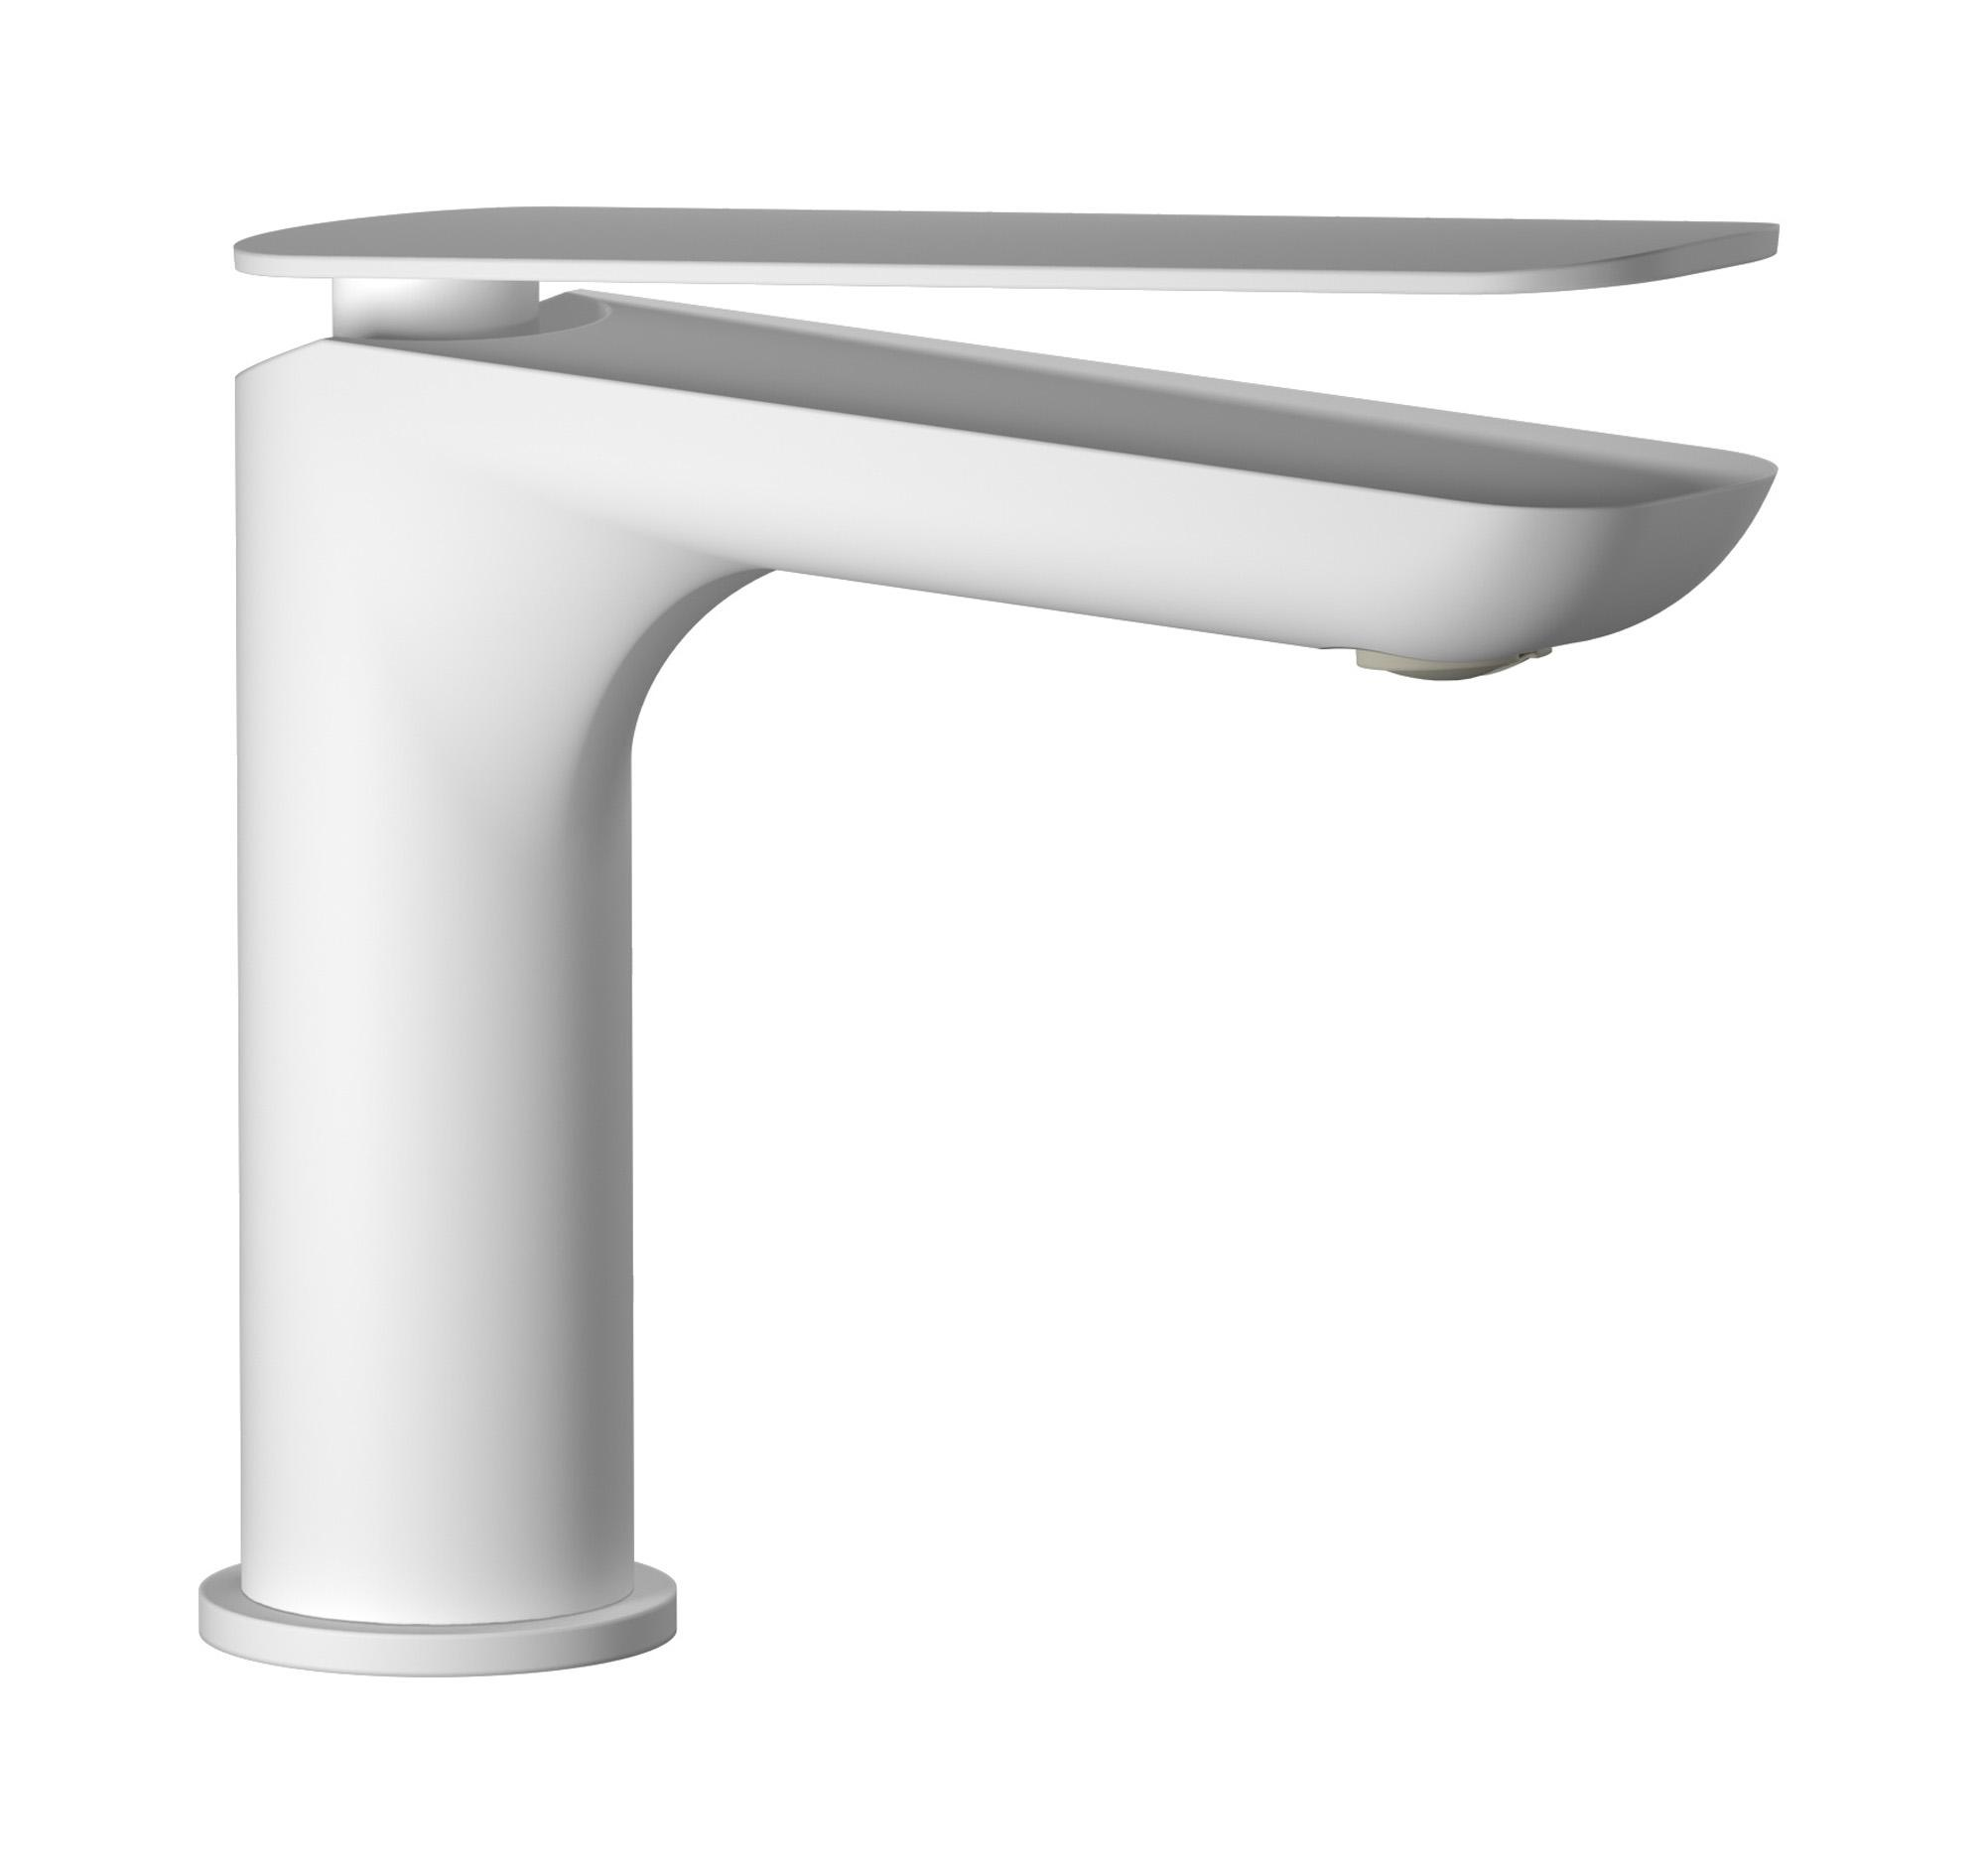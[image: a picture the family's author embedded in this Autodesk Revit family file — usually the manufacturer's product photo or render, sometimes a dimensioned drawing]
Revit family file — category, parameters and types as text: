
# Revit family: K2200
name_source: partatom
category: Apparecchi idraulici
units: mm (PartAtom-declared; Revit-internal decimal feet)

## family parameters
Basato su piano di lavoro = No
Condiviso = No
Mantieni orientamento annotazione = No
Numero OmniClass = 23.45.55.17
Punto di calcolo locali = No
Quota connettore circolare = Usa diametro
Sempre verticale = Sì
Taglio con vuoti quando caricato = No
Tipo di parte = Normale
Titolo OmniClass = Mixing Faucets

## types (9) — shared parameters
Cold water inlet = 10 mm  [stored 0.0328084 ft]
Commenti sul tipo = Washbasin mixer
Connessione CW = No
Connessione HW = No
Connessione di scarico = No
Connessione di ventilazione = No
Descrizione = Monohole washbasin mixer complete with drain
Hot water inlet = 10 mm  [stored 0.0328084 ft]
Produttore = IB Rubinetterie S.p.A.
URL = https://www.weareib.it
zero-valued in all types: Prospetto di default

## per-type parameters (varying)
| type | Finishes surface | Immagine tipo | Modello |
| Chrome | IB_Chrome | K2200CC.jpg | K2200CC |
| Brushed nickel | IB_Brushed nickel | K2200SS.jpg | K2200SS |
| Platinum | IB_Platinum | K2200PL.jpg | K2200PL |
| Matt white | IB_matt white | K2200BO.jpg | K2200BO |
| Matt black | IB_matt black | K2200NP.jpg | K2200NP |
| Pale gold | IB_Pale gold | K2200II.jpg | K2200II |
| Brushed pale gold | IB_brushed pale gold | K2200IS.jpg | K2200IS |
| Rose gold | IB_Rose gold | K2200RS.jpg | K2200RS |
| Gold | IB_gold | K2200OO.jpg | K2200OO |

note: [stored X ft] marks values corroborated as IEEE doubles in the binary element streams (Revit-internal decimal feet)
